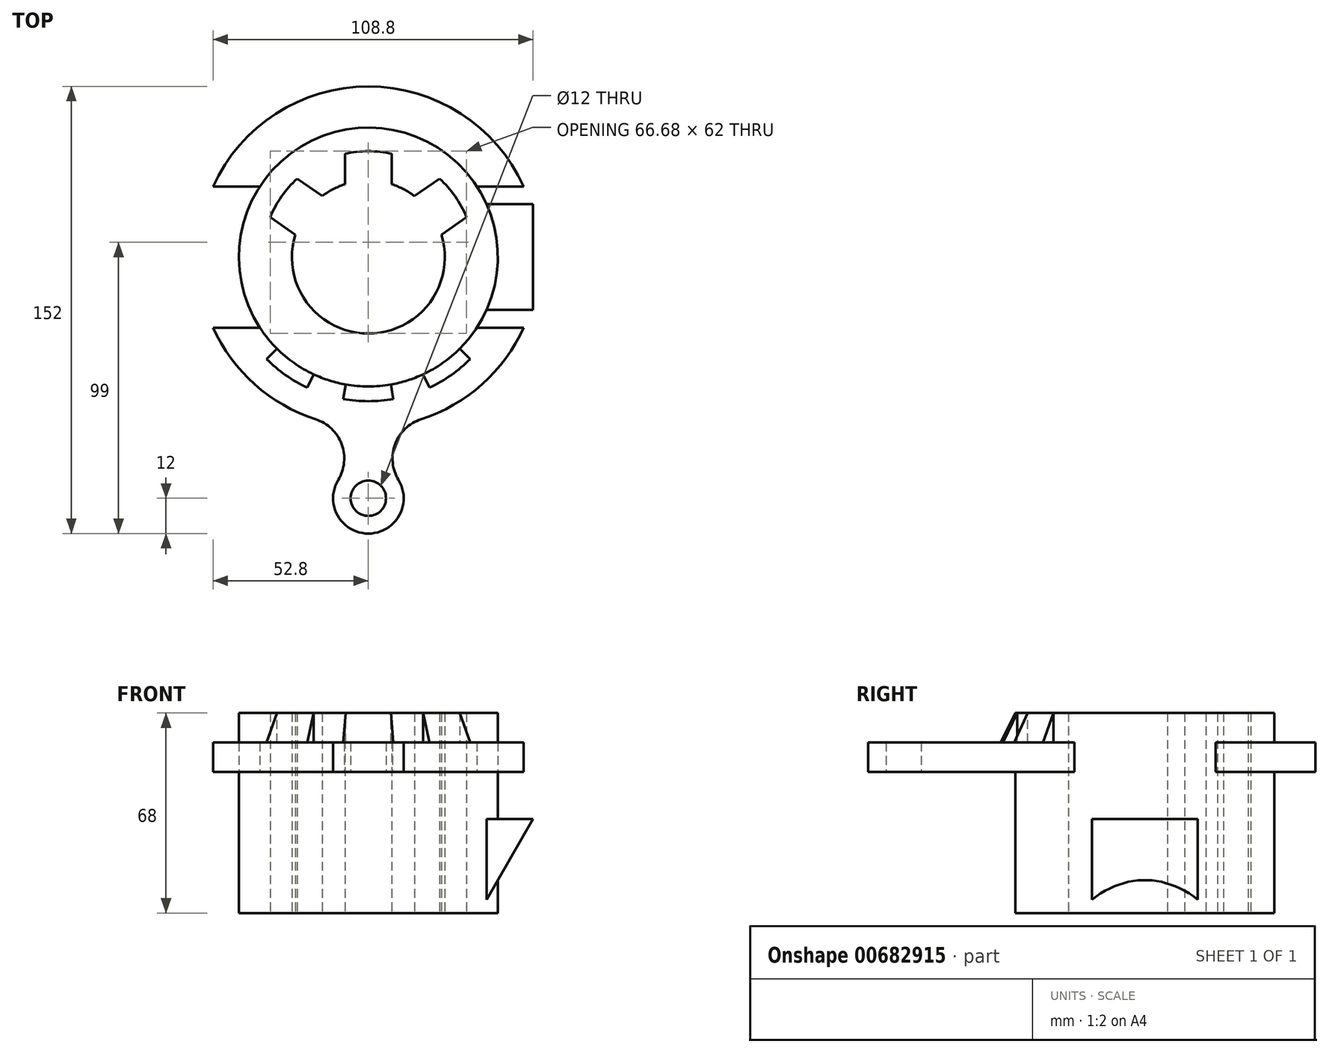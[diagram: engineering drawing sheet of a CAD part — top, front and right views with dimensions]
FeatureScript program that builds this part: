
annotation { "Feature Type Name" : "Feature", "Feature Type Description" : "" }
export const myFeature = defineFeature(function(context is Context, id is Id, definition is map)
    precondition{}
    {
        {
            var Q0;
            Q0=qCreatedBy(makeId("Top.planeOp"),FACE);
            var sketch = newSketch(context, id + "F0", { "sketchPlane" : qUnion([Q0])});
            skLineSegment(sketch, "E0", {"start": v(0, 50.47) * mm, "end": v(0, 36) * mm, "construction": true});
            skCircle(sketch, "E1", {"center": v(0, 0) * mm, "radius": 44 * mm});
            skArc(sketch, "E2", {"start": v(-24.16, 26.69) * mm, "mid": v(-29.49, 20.65) * mm, "end": v(-33.34, 13.58) * mm});
            skArc(sketch, "E3", {"start": v(-8, 24.74) * mm, "mid": v(-12, 23.06) * mm, "end": v(-15.68, 20.74) * mm});
            skLineSegment(sketch, "E4.0", {"start": v(-8, 50.47) * mm, "end": v(-8, -55.45) * mm, "construction": true});
            skLineSegment(sketch, "E5.0", {"start": v(8, 50.47) * mm, "end": v(8, -55.45) * mm, "construction": true});
            skLineSegment(sketch, "E6", {"start": v(8, 24.74) * mm, "end": v(8, 35.1) * mm});
            skLineSegment(sketch, "E7", {"start": v(-8, 24.74) * mm, "end": v(-8, 35.1) * mm});
            skLineSegment(sketch, "E8.trimOffspring", {"start": v(0, 0) * mm, "end": v(0, -55.45) * mm, "construction": true});
            skLineSegment(sketch, "E9", {"start": v(0, 0) * mm, "end": v(44.11, 30.89) * mm, "construction": true});
            skLineSegment(sketch, "E10.0", {"start": v(4.59, -6.55) * mm, "end": v(48.7, 24.34) * mm, "construction": true});
            skLineSegment(sketch, "E11.0", {"start": v(-4.59, 6.55) * mm, "end": v(39.53, 37.44) * mm, "construction": true});
            skLineSegment(sketch, "E12", {"start": v(15.68, 20.74) * mm, "end": v(24.16, 26.69) * mm});
            skLineSegment(sketch, "E13", {"start": v(24.85, 7.64) * mm, "end": v(33.34, 13.58) * mm});
            skLineSegment(sketch, "E14.MirrorCS", {"start": v(4.59, 6.55) * mm, "end": v(-39.53, 37.44) * mm, "construction": true});
            skLineSegment(sketch, "E15.MirrorCS", {"start": v(-4.59, -6.55) * mm, "end": v(-48.7, 24.34) * mm, "construction": true});
            skLineSegment(sketch, "E16", {"start": v(-15.68, 20.74) * mm, "end": v(-24.16, 26.69) * mm});
            skLineSegment(sketch, "E17", {"start": v(-24.85, 7.64) * mm, "end": v(-33.34, 13.58) * mm});
            skArc(sketch, "E18.trimOffspring", {"start": v(-24.85, 7.64) * mm, "mid": v(0, -26) * mm, "end": v(24.85, 7.64) * mm});
            skArc(sketch, "E19.trimOffspring", {"start": v(15.68, 20.74) * mm, "mid": v(12, 23.06) * mm, "end": v(8, 24.74) * mm});
            skArc(sketch, "E20.trimOffspring", {"start": v(8, 35.1) * mm, "mid": v(0, 36) * mm, "end": v(-8, 35.1) * mm});
            skArc(sketch, "E21.trimOffspring", {"start": v(33.34, 13.58) * mm, "mid": v(29.49, 20.65) * mm, "end": v(24.16, 26.69) * mm});
            skSolve(sketch);
        }
        {
            var Q0;
            Q0=makeQuery(id+"F0.imprint","IMPRINT",FACE,{"disambiguationData":[TD([[makeQuery(id+"F0.imprint","IMPRINT",EDGE,{"derivedFrom":sQuery(id+"F0.wireOp",EDGE,"E1")}),1.0]])]});
            extrude(context, id + "F1", {"entities" : qUnion([Q0]), "depth" : 68 * mm, "offsetDistance" : 25 * mm});
        }
        {
            var Q0;
            Q0=makeQuery(id+"F1.opExtrude","CAP_FACE",FACE,{"disambiguationData":[OSD([sQuery(id+"F0.wireOp",EDGE,"E1"),sQuery(id+"F0.wireOp",EDGE,"E2"),sQuery(id+"F0.wireOp",EDGE,"E3"),sQuery(id+"F0.wireOp",EDGE,"E6"),sQuery(id+"F0.wireOp",EDGE,"E7"),sQuery(id+"F0.wireOp",EDGE,"E12"),sQuery(id+"F0.wireOp",EDGE,"E13"),sQuery(id+"F0.wireOp",EDGE,"E16"),sQuery(id+"F0.wireOp",EDGE,"E17"),sQuery(id+"F0.wireOp",EDGE,"E18.trimOffspring"),sQuery(id+"F0.wireOp",EDGE,"E19.trimOffspring"),sQuery(id+"F0.wireOp",EDGE,"E20.trimOffspring"),sQuery(id+"F0.wireOp",EDGE,"E21.trimOffspring")])],"isStart":false});
            cPlane(context, id + "F2", {"entities" : qUnion([Q0]), "cplaneType" : CPlaneType.OFFSET, "offset" : 20 * mm, "oppositeDirection" : true, "width" : 150 * mm, "height" : 150 * mm});
        }
        {
            var Q0;
            Q0=qCreatedBy(id+"F2.planeOp",FACE);
            var sketch = newSketch(context, id + "F3", { "sketchPlane" : qUnion([Q0])});
            skArc(sketch, "E22", {"start": v(-52.8, -24) * mm, "mid": v(-38.63, -43.26) * mm, "end": v(-17.9, -55.17) * mm});
            skLineSegment(sketch, "E23", {"start": v(0, 0) * mm, "end": v(0, -82) * mm, "construction": true});
            skCircle(sketch, "E24", {"center": v(0, -82) * mm, "radius": 6 * mm});
            skArc(sketch, "E25", {"start": v(-10.25, -75.76) * mm, "mid": v(0, -94) * mm, "end": v(10.25, -75.76) * mm});
            skLineSegment(sketch, "E26", {"start": v(-58, 0) * mm, "end": v(58, 0) * mm, "construction": true});
            skLineSegment(sketch, "E27.0", {"start": v(-52.8, -24) * mm, "end": v(-36.88, -24) * mm});
            skLineSegment(sketch, "E28.0", {"start": v(-52.8, 24) * mm, "end": v(-36.88, 24) * mm});
            skArc(sketch, "E29.trimOffspring", {"start": v(52.8, 24) * mm, "mid": v(0, 58) * mm, "end": v(-52.8, 24) * mm});
            skCircle(sketch, "E30.0", {"center": v(0, 0) * mm, "radius": 44 * mm});
            skLineSegment(sketch, "E31.trimOffspring", {"start": v(36.88, -24) * mm, "end": v(52.8, -24) * mm});
            skLineSegment(sketch, "E32.trimOffspring", {"start": v(36.88, 24) * mm, "end": v(52.8, 24) * mm});
            skArc(sketch, "E33.trimOffspring", {"start": v(20.94, -54.09) * mm, "mid": v(39.82, -42.17) * mm, "end": v(52.8, -24) * mm});
            skArc(sketch, "E34", {"start": v(17.9, -55.17) * mm, "mid": v(9.09, -63.62) * mm, "end": v(10.25, -75.76) * mm});
            skArc(sketch, "E35", {"start": v(-10.25, -75.76) * mm, "mid": v(-9.09, -63.62) * mm, "end": v(-17.9, -55.17) * mm});
            skArc(sketch, "E36.trimOffspring", {"start": v(17.9, -55.17) * mm, "mid": v(19.43, -54.65) * mm, "end": v(20.94, -54.09) * mm});
            skSolve(sketch);
        }
        {
            var Q0;
            Q0=makeQuery(id+"F3.imprint","IMPRINT",FACE,{"disambiguationData":[TD([[makeQuery(id+"F3.imprint","IMPRINT",EDGE,{"derivedFrom":sQuery(id+"F3.wireOp",EDGE,"E22")}),1.0]])]});
            var Q1;
            {var subQ0=sQuery(id+"F3.wireOp",EDGE,"E28.0");Q1=makeQuery(id+"F3.imprint","IMPRINT",FACE,{"disambiguationData":[TD([[makeQuery(id+"F3.imprint","IMPRINT",EDGE,{"derivedFrom":subQ0}),1.0]])]});}
            extrude(context, id + "F4", {"entities" : qUnion([Q0, Q1]), "operationType" : NewBodyOperationType.ADD, "depth" : 10 * mm, "offsetDistance" : 25 * mm});
        }
        {
            var Q0;
            Q0=qCreatedBy(makeId("Front.planeOp"),FACE);
            var sketch = newSketch(context, id + "F5", { "sketchPlane" : qUnion([Q0])});
            skLineSegment(sketch, "E37", {"start": v(44, 68) * mm, "end": v(44, 0) * mm, "construction": true});
            skLineSegment(sketch, "E38.0", {"start": v(-44, 0) * mm, "end": v(44, 0) * mm, "construction": true});
            skLineSegment(sketch, "E39.0", {"start": v(39, 32) * mm, "end": v(56, 32) * mm});
            skLineSegment(sketch, "E40.0", {"start": v(56, 68) * mm, "end": v(56, 0) * mm, "construction": true});
            skLineSegment(sketch, "E41", {"start": v(56, 32) * mm, "end": v(39, 2.56) * mm});
            skLineSegment(sketch, "E42.0", {"start": v(39, 68) * mm, "end": v(39, 0) * mm, "construction": true});
            skLineSegment(sketch, "E43", {"start": v(39, 32) * mm, "end": v(39, 2.56) * mm});
            skSolve(sketch);
        }
        {
            var Q0;
            Q0=makeQuery(id+"F5.imprint","IMPRINT",FACE,{"disambiguationData":[TD([[makeQuery(id+"F5.imprint","IMPRINT",EDGE,{"derivedFrom":sQuery(id+"F5.wireOp",EDGE,"E39.0")}),-1.0]])]});
            extrude(context, id + "F6", {"entities" : qUnion([Q0]), "operationType" : NewBodyOperationType.ADD, "endBound" : BoundingType.SYMMETRIC, "depth" : 36 * mm, "offsetDistance" : 25 * mm});
        }
        {
            var Q0;
            Q0=qCreatedBy(makeId("Right.planeOp"),FACE);
            var sketch = newSketch(context, id + "F7", { "sketchPlane" : qUnion([Q0])});
            skLineSegment(sketch, "E44.0.0", {"start": v(-75.76, 58) * mm, "end": v(-94, 58) * mm, "construction": true});
            skLineSegment(sketch, "E44.0.1", {"start": v(-75.76, 58) * mm, "end": v(-60.9, 58) * mm, "construction": true});
            skLineSegment(sketch, "E44.0.2", {"start": v(-60.9, 58) * mm, "end": v(-54.09, 58) * mm, "construction": true});
            skLineSegment(sketch, "E44.0.3", {"start": v(-54.09, 58) * mm, "end": v(-24, 58) * mm, "construction": true});
            skLineSegment(sketch, "E44.0.5", {"start": v(-24, 58) * mm, "end": v(-44, 58) * mm, "construction": true});
            skLineSegment(sketch, "E44.0.7", {"start": v(-24, 58) * mm, "end": v(-24, 58) * mm});
            skLineSegment(sketch, "E44.0.8", {"start": v(-24, 58) * mm, "end": v(-37.06, 58) * mm, "construction": true});
            skLineSegment(sketch, "E44.0.9", {"start": v(-37.06, 58) * mm, "end": v(-51.91, 58) * mm, "construction": true});
            skLineSegment(sketch, "E45", {"start": v(-44, 0) * mm, "end": v(-44, 68) * mm, "construction": true});
            skPoint(sketch, "E46.0", {"position": v(0, 0) * mm});
            skLineSegment(sketch, "E47", {"start": v(-44, 68) * mm, "end": v(-49, 58) * mm});
            skLineSegment(sketch, "E48", {"start": v(-49, 58) * mm, "end": v(-44, 58) * mm});
            skLineSegment(sketch, "E49", {"start": v(-44, 58) * mm, "end": v(-44, 68) * mm});
            skLineSegment(sketch, "E50", {"start": v(0, 0) * mm, "end": v(0, 73.61) * mm, "construction": true});
            skSolve(sketch);
        }
        {
            var Q0;
            Q0=makeQuery(id+"F7.imprint","IMPRINT",FACE,{"disambiguationData":[TD([[makeQuery(id+"F7.imprint","IMPRINT",EDGE,{"derivedFrom":sQuery(id+"F7.wireOp",EDGE,"E47")}),1.0]])]});
            var Q1;
            Q1=sQuery(id+"F7.wireOp",EDGE,"E50");
            revolve(context, id + "F8", {"operationType" : NewBodyOperationType.ADD, "entities" : qUnion([Q0]), "axis" : qUnion([Q1]), "revolveType" : RevolveType.TWO_DIRECTIONS, "angle" : 10 * degree, "angleBack" : 350 * degree});
        }
        {
            var Q0;
            Q0=sQuery(id+"F7.wireOp",EDGE,"E50");
            cPlane(context, id + "F9", {"entities" : qUnion([Q0]), "cplaneType" : CPlaneType.LINE_ANGLE, "offset" : 25 * mm, "angle" : 35 * degree, "width" : 150 * mm, "height" : 150 * mm});
        }
        {
            var Q0;
            Q0=sQuery(id+"F7.wireOp",EDGE,"E50");
            cPlane(context, id + "F10", {"entities" : qUnion([Q0]), "cplaneType" : CPlaneType.LINE_ANGLE, "offset" : 25 * mm, "angle" : 325 * degree, "width" : 150 * mm, "height" : 150 * mm});
        }
        {
            var Q0;
            Q0=qCreatedBy(id+"F9.planeOp",FACE);
            var sketch = newSketch(context, id + "F11", { "sketchPlane" : qUnion([Q0])});
            skLineSegment(sketch, "E51", {"start": v(-44, 0) * mm, "end": v(-44, 68) * mm, "construction": true});
            skLineSegment(sketch, "E52", {"start": v(-44, 68) * mm, "end": v(-44, 58) * mm});
            skLineSegment(sketch, "E53", {"start": v(-49, 58) * mm, "end": v(-44, 68) * mm});
            skLineSegment(sketch, "E54", {"start": v(-49, 58) * mm, "end": v(-44, 58) * mm});
            skLineSegment(sketch, "E55.0", {"start": v(0, 0) * mm, "end": v(0, 73.61) * mm, "construction": true});
            skSolve(sketch);
        }
        {
            var Q0;
            Q0=makeQuery(id+"F11.imprint","IMPRINT",FACE,{"disambiguationData":[TD([[makeQuery(id+"F11.imprint","IMPRINT",EDGE,{"derivedFrom":sQuery(id+"F11.wireOp",EDGE,"E52")}),-1.0]])]});
            var Q1;
            Q1=sQuery(id+"F11.wireOp",EDGE,"E55.0");
            revolve(context, id + "F12", {"operationType" : NewBodyOperationType.ADD, "entities" : qUnion([Q0]), "axis" : qUnion([Q1]), "revolveType" : RevolveType.SYMMETRIC, "angle" : 20 * degree});
        }
        {
            var Q0;
            Q0=qCreatedBy(id+"F10.planeOp",FACE);
            var sketch = newSketch(context, id + "F13", { "sketchPlane" : qUnion([Q0])});
            skLineSegment(sketch, "E56.0.6", {"start": v(-44.4, 58) * mm, "end": v(-39.88, 58) * mm, "construction": true});
            skLineSegment(sketch, "E57", {"start": v(-44, 0) * mm, "end": v(-44, 68) * mm, "construction": true});
            skLineSegment(sketch, "E58", {"start": v(-44, 58) * mm, "end": v(-44, 68) * mm});
            skLineSegment(sketch, "E59", {"start": v(-44, 68) * mm, "end": v(-49, 58) * mm});
            skLineSegment(sketch, "E60", {"start": v(-49, 58) * mm, "end": v(-44, 58) * mm});
            skSolve(sketch);
        }
        {
            var Q0;
            Q0=makeQuery(id+"F13.imprint","IMPRINT",FACE,{"disambiguationData":[TD([[makeQuery(id+"F13.imprint","IMPRINT",EDGE,{"derivedFrom":sQuery(id+"F13.wireOp",EDGE,"E58")}),1.0]])]});
            var Q1;
            Q1=sQuery(id+"F7.wireOp",EDGE,"E50");
            revolve(context, id + "F14", {"operationType" : NewBodyOperationType.ADD, "entities" : qUnion([Q0]), "axis" : qUnion([Q1]), "revolveType" : RevolveType.SYMMETRIC, "angle" : 20 * degree});
        }
    });
